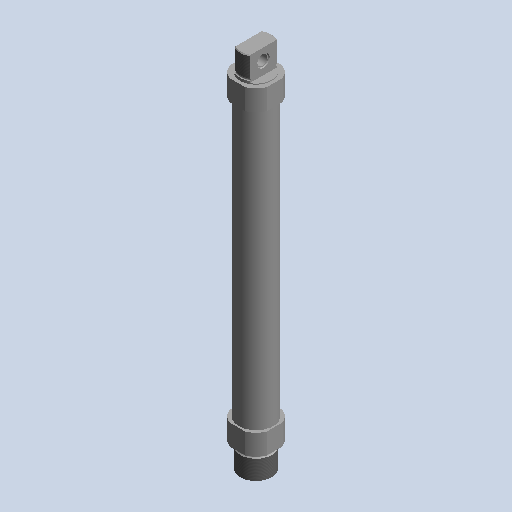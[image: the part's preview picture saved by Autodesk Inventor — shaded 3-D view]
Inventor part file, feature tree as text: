
AUTODESK INVENTOR PART (.ipt)
format: ipt  version: 2022 (Build 260153000, 153)  size: 248,320 bytes
history: native  units: mm (DEFAULTED — no unit token found)
features: other x70, sketch x7, revolve x3, thread x2, extrude x2, hole x2
ambient origin geometry x8: Origin, YZ Plane, XZ Plane, XY Plane, X Axis, Y Axis, Z Axis, Center Point
bodies: Solid1 (feature_tree)
feature tree (86):
  revolve  "Revolution1"  [1 undecoded]
  thread  "Thread1"  [1 undecoded]
  thread  "Thread2"  [1 undecoded]
  extrude  "Extrusion1"  TaperAngle=360.0deg  [1 undecoded]
  extrude  "Extrusion2"  TaperAngle=360.0deg  [1 undecoded]
  revolve  "Revolution2"  [1 undecoded]
  hole  "Hole1"  [1 undecoded]
  hole  "Hole2"  [1 undecoded]
  revolve  "Revolution3"  [1 undecoded]
  other  "FDT_FRONT_XY"
  other  "FDT_FRONT_YZ"
  other  "FDT_FRONT_ZX"
  other  "FDT_FRONT_X"
  other  "FDT_FRONT_Y"
  other  "FDT_FRONT_Z"
  other  "FDT_FRONT_Center"
  other  "FDT_QSFRONT_XY"
  other  "FDT_QSFRONT_YZ"
  other  "FDT_QSFRONT_ZX"
  other  "FDT_QSFRONT_X"
  other  "FDT_QSFRONT_Y"
  other  "FDT_QSFRONT_Z"
  other  "FDT_QSFRONT_Center"
  other  "FDT_QSREAR_XY"
  other  "FDT_QSREAR_YZ"
  other  "FDT_QSREAR_ZX"
  other  "FDT_QSREAR_X"
  other  "FDT_QSREAR_Y"
  other  "FDT_QSREAR_Z"
  other  "FDT_QSREAR_Center"
  other  "FDT_REAR_XY"
  other  "FDT_REAR_YZ"
  other  "FDT_REAR_ZX"
  other  "FDT_REAR_X"
  other  "FDT_REAR_Y"
  other  "FDT_REAR_Z"
  other  "FDT_REAR_Center"
  other  "FDT_SMBR1_XY"
  other  "FDT_SMBR1_YZ"
  other  "FDT_SMBR1_ZX"
  other  "FDT_SMBR1_X"
  other  "FDT_SMBR1_Y"
  other  "FDT_SMBR1_Z"
  other  "FDT_SMBR1_Center"
  other  "FDT_SMBR2_XY"
  other  "FDT_SMBR2_YZ"
  other  "FDT_SMBR2_ZX"
  other  "FDT_SMBR2_X"
  other  "FDT_SMBR2_Y"
  other  "FDT_SMBR2_Z"
  other  "FDT_SMBR2_Center"
  other  "FDT_SWIVELAXIS_XY"
  other  "FDT_SWIVELAXIS_YZ"
  other  "FDT_SWIVELAXIS_ZX"
  other  "FDT_SWIVELAXIS_X"
  other  "FDT_SWIVELAXIS_Y"
  other  "FDT_SWIVELAXIS_Z"
  other  "FDT_SWIVELAXIS_Center"
  other  "NUT_XY"
  other  "NUT_YZ"
  other  "NUT_ZX"
  other  "NUT_X"
  other  "NUT_Y"
  other  "NUT_Z"
  other  "NUT_Center"
  other  "ZR_XY"
  other  "ZR_YZ"
  other  "ZR_ZX"
  other  "ZR_X"
  other  "ZR_Y"
  other  "ZR_Z"
  other  "ZR_Center"
  other  "ZYL_XY"
  other  "ZYL_YZ"
  other  "ZYL_ZX"
  other  "ZYL_X"
  other  "ZYL_Y"
  other  "ZYL_Z"
  other  "ZYL_Center"
  sketch  "Sketch_12"  dims[d25=0.0mm d26=0.0mm d27=0.0mm d28=0.0mm d29=0.0mm d30=0.0mm]
  sketch  "Sketch_1"  dims[d0=360.0deg d1=23.03mm d2=0.0mm d3=23.03mm d4=0.0mm d5=453.6mm d6=0.0mm]
  sketch  "Sketch_124"
  sketch  "Sketch_3"  dims[d7=46.0mm d8=0.0mm d9=360.0deg]
  sketch  "Sketch5"  dims[d10=11.445mm d11=15.856mm d12=13.157mm d13=2.0mm d14=90.0deg d15=22.5mm d16=0.0mm]
  sketch  "Sketch6"  dims[d17=11.445mm d18=9.856mm d19=13.157mm d20=2.0mm d21=90.0deg d22=10.5mm d23=120.0deg d24=360.0deg]
  sketch  "Sketch_129"
note: 9 required parameter values undecoded (feature->parameter linkage not recoverable at this tier; creation-order binding heuristic only, values carry confidence <= 0.55)